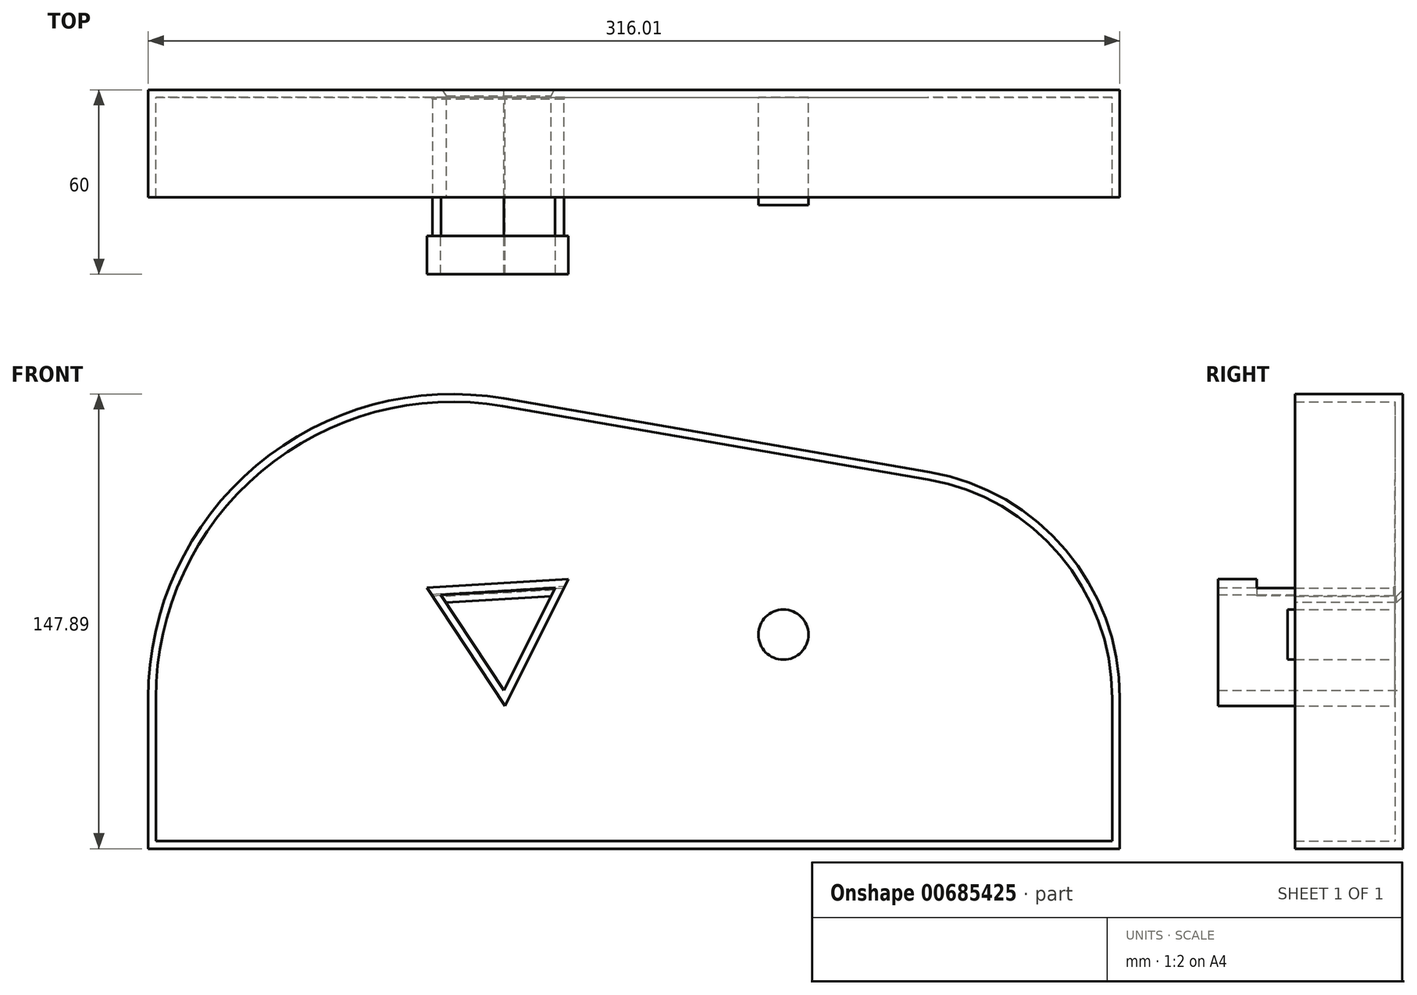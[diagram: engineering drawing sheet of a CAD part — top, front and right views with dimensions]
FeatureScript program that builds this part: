
annotation { "Feature Type Name" : "Feature", "Feature Type Description" : "" }
export const myFeature = defineFeature(function(context is Context, id is Id, definition is map)
    precondition{}
    {
        {
            var Q0;
            Q0=qCreatedBy(makeId("Front.planeOp"),FACE);
            var sketch = newSketch(context, id + "F0", { "sketchPlane" : qUnion([Q0])});
            skCircle(sketch, "E0", {"center": v(0, 0) * mm, "radius": 53.72 * mm});
            skCircle(sketch, "E1", {"center": v(0, 0) * mm, "radius": 58.67 * mm, "construction": true});
            skCircle(sketch, "E2", {"center": v(0, 0) * mm, "radius": 63.5 * mm, "construction": true});
            skLineSegment(sketch, "E3", {"start": v(0, 0) * mm, "end": v(0, 95.44) * mm, "construction": true});
            skLineSegment(sketch, "E4", {"start": v(0, 0) * mm, "end": v(-6.27, 95.6) * mm, "construction": true});
            skLineSegment(sketch, "E5", {"start": v(0, 58.67) * mm, "end": v(-75.4, 58.67) * mm, "construction": true});
            skLineSegment(sketch, "E6", {"start": v(0, 58.67) * mm, "end": v(-75.03, 31.36) * mm, "construction": true});
            skCircle(sketch, "E7", {"center": v(0, 0) * mm, "radius": 55.14 * mm, "construction": true});
            skCircle(sketch, "E8", {"center": v(0, 58.67) * mm, "radius": 14.6 * mm, "construction": true});
            skCircle(sketch, "E9", {"center": v(-13.72, 53.68) * mm, "radius": 14.6 * mm, "construction": true});
            skArc(sketch, "E10", {"start": v(0, 58.67) * mm, "mid": v(-1.15, 61.22) * mm, "end": v(-2.86, 63.44) * mm});
            skArc(sketch, "E11", {"start": v(0.88, 53.71) * mm, "mid": v(0.6, 56.22) * mm, "end": v(0, 58.67) * mm});
            skArc(sketch, "E12.MirrorCS", {"start": v(-7.66, 58.17) * mm, "mid": v(-6.85, 60.85) * mm, "end": v(-5.45, 63.27) * mm});
            skArc(sketch, "E13.MirrorCS", {"start": v(-7.88, 53.14) * mm, "mid": v(-7.94, 55.66) * mm, "end": v(-7.66, 58.17) * mm});
            skArc(sketch, "E14", {"start": v(-2.86, 63.44) * mm, "mid": v(-4.17, 63.7) * mm, "end": v(-5.45, 63.27) * mm});
            skCircle(sketch, "E15", {"center": v(0, 0) * mm, "radius": 30.86 * mm});
            skCircle(sketch, "E16.cCircle", {"center": v(0, 0) * mm, "radius": 10.79 * mm, "construction": true});
            skLineSegment(sketch, "E16.0", {"start": v(18.01, 11.88) * mm, "end": v(1.28, -21.54) * mm});
            skLineSegment(sketch, "E16.1", {"start": v(1.28, -21.54) * mm, "end": v(-19.3, 9.66) * mm});
            skLineSegment(sketch, "E16.2", {"start": v(-19.3, 9.66) * mm, "end": v(18.01, 11.88) * mm});
            skPoint(sketch, "E16.0.midPoint", {"position": v(9.65, -4.83) * mm});
            skSolve(sketch);
        }
        {
            var Q0;
            {var subQ0=sQuery(id+"F0.wireOp",EDGE,"E0");var subQ1=makeQuery(id+"F0.imprint","INTERSECT",VERTEX,{"derivedFrom":[subQ0,sQuery(id+"F0.wireOp",EDGE,"E11")]});Q0=makeQuery(id+"F0.imprint","IMPRINT",FACE,{"disambiguationData":[TD([[makeQuery(id+"F0.imprint","IMPRINT",EDGE,{"disambiguationData":[TD([[subQ1,-1.0]])],"derivedFrom":subQ0}),1.0]])]});}
            var Q1;
            Q1=makeQuery(id+"F0.imprint","IMPRINT",FACE,{"disambiguationData":[TD([[makeQuery(id+"F0.imprint","IMPRINT",EDGE,{"derivedFrom":sQuery(id+"F0.wireOp",EDGE,"E10")}),1.0]])]});
            var Q2;
            Q2=makeQuery(id+"F0.imprint","IMPRINT",FACE,{"disambiguationData":[TD([[makeQuery(id+"F0.imprint","IMPRINT",EDGE,{"derivedFrom":sQuery(id+"F0.wireOp",EDGE,"3Q0PKgbY-dWzt-37Ak-rDaJ-mU9UwyPIQOex")}),1.0]])]});
            var Q3;
            Q3=makeQuery(id+"F0.imprint","IMPRINT",FACE,{"disambiguationData":[TD([[makeQuery(id+"F0.imprint","IMPRINT",EDGE,{"derivedFrom":sQuery(id+"F0.wireOp",EDGE,"4417614c-5319-454a-a1dd-4df527e49696.0")}),-1.0]])]});
            extrude(context, id + "F1", {"entities" : qUnion([Q0, Q1, Q2, Q3]), "depth" : 30 * mm, "offsetDistance" : 25 * mm});
        }
        {
            var Q0;
            Q0=makeQuery(id+"F0.imprint","IMPRINT",FACE,{"disambiguationData":[TD([[makeQuery(id+"F0.imprint","IMPRINT",EDGE,{"derivedFrom":sQuery(id+"F0.wireOp",EDGE,"E15")}),1.0]])]});
            extrude(context, id + "F2", {"entities" : qUnion([Q0]), "operationType" : NewBodyOperationType.ADD, "depth" : 50 * mm, "offsetDistance" : 25 * mm});
        }
        {
            var Q0;
            Q0=makeQuery(id+"F1.opExtrude","CAP_EDGE",EDGE,{"disambiguationData":[OSD([sQuery(id+"F0.wireOp",EDGE,"E11")])],"isStart":false});
            var Q1;
            Q1=makeQuery(id+"F1.opExtrude","CAP_EDGE",EDGE,{"disambiguationData":[OSD([sQuery(id+"F0.wireOp",EDGE,"E13.MirrorCS")])],"isStart":false});
            var Q2;
            Q2=makeQuery(id+"F18UF4900IuEQJn_1.opPattern","COPY",EDGE,{"derivedFrom":makeQuery(id+"F1.opExtrude","CAP_EDGE",EDGE,{"disambiguationData":[OSD([sQuery(id+"F0.wireOp",EDGE,"E13.MirrorCS")])],"isStart":false}),"instanceName":"1"});
            var Q3;
            Q3=makeQuery(id+"F18UF4900IuEQJn_1.opPattern","COPY",EDGE,{"derivedFrom":makeQuery(id+"F1.opExtrude","CAP_EDGE",EDGE,{"disambiguationData":[OSD([sQuery(id+"F0.wireOp",EDGE,"E11")])],"isStart":false}),"instanceName":"1"});
            var Q4;
            Q4=makeQuery(id+"F18UF4900IuEQJn_1.opPattern","COPY",EDGE,{"derivedFrom":makeQuery(id+"F1.opExtrude","CAP_EDGE",EDGE,{"disambiguationData":[OSD([sQuery(id+"F0.wireOp",EDGE,"E13.MirrorCS")])],"isStart":false}),"instanceName":"2"});
            var Q5;
            Q5=makeQuery(id+"F18UF4900IuEQJn_1.opPattern","COPY",EDGE,{"derivedFrom":makeQuery(id+"F1.opExtrude","CAP_EDGE",EDGE,{"disambiguationData":[OSD([sQuery(id+"F0.wireOp",EDGE,"E11")])],"isStart":false}),"instanceName":"2"});
            var Q6;
            Q6=makeQuery(id+"F18UF4900IuEQJn_1.opPattern","COPY",EDGE,{"derivedFrom":makeQuery(id+"F1.opExtrude","CAP_EDGE",EDGE,{"disambiguationData":[OSD([sQuery(id+"F0.wireOp",EDGE,"E13.MirrorCS")])],"isStart":false}),"instanceName":"3"});
            var Q7;
            Q7=makeQuery(id+"F18UF4900IuEQJn_1.opPattern","COPY",EDGE,{"derivedFrom":makeQuery(id+"F1.opExtrude","CAP_EDGE",EDGE,{"disambiguationData":[OSD([sQuery(id+"F0.wireOp",EDGE,"E11")])],"isStart":false}),"instanceName":"3"});
            var Q8;
            Q8=makeQuery(id+"F18UF4900IuEQJn_1.opPattern","COPY",EDGE,{"derivedFrom":makeQuery(id+"F1.opExtrude","CAP_EDGE",EDGE,{"disambiguationData":[OSD([sQuery(id+"F0.wireOp",EDGE,"E13.MirrorCS")])],"isStart":false}),"instanceName":"4"});
            var Q9;
            Q9=makeQuery(id+"F18UF4900IuEQJn_1.opPattern","COPY",EDGE,{"derivedFrom":makeQuery(id+"F1.opExtrude","CAP_EDGE",EDGE,{"disambiguationData":[OSD([sQuery(id+"F0.wireOp",EDGE,"E11")])],"isStart":false}),"instanceName":"4"});
            var Q10;
            Q10=makeQuery(id+"F18UF4900IuEQJn_1.opPattern","COPY",EDGE,{"derivedFrom":makeQuery(id+"F1.opExtrude","CAP_EDGE",EDGE,{"disambiguationData":[OSD([sQuery(id+"F0.wireOp",EDGE,"E13.MirrorCS")])],"isStart":false}),"instanceName":"5"});
            var Q11;
            Q11=makeQuery(id+"F18UF4900IuEQJn_1.opPattern","COPY",EDGE,{"derivedFrom":makeQuery(id+"F1.opExtrude","CAP_EDGE",EDGE,{"disambiguationData":[OSD([sQuery(id+"F0.wireOp",EDGE,"E11")])],"isStart":false}),"instanceName":"5"});
            var Q12;
            Q12=makeQuery(id+"F18UF4900IuEQJn_1.opPattern","COPY",EDGE,{"derivedFrom":makeQuery(id+"F1.opExtrude","CAP_EDGE",EDGE,{"disambiguationData":[OSD([sQuery(id+"F0.wireOp",EDGE,"E13.MirrorCS")])],"isStart":false}),"instanceName":"6"});
            var Q13;
            Q13=makeQuery(id+"F18UF4900IuEQJn_1.opPattern","COPY",EDGE,{"derivedFrom":makeQuery(id+"F1.opExtrude","CAP_EDGE",EDGE,{"disambiguationData":[OSD([sQuery(id+"F0.wireOp",EDGE,"E11")])],"isStart":false}),"instanceName":"6"});
            var Q14;
            Q14=makeQuery(id+"F18UF4900IuEQJn_1.opPattern","COPY",EDGE,{"derivedFrom":makeQuery(id+"F1.opExtrude","CAP_EDGE",EDGE,{"disambiguationData":[OSD([sQuery(id+"F0.wireOp",EDGE,"E13.MirrorCS")])],"isStart":false}),"instanceName":"7"});
            var Q15;
            Q15=makeQuery(id+"F18UF4900IuEQJn_1.opPattern","COPY",EDGE,{"derivedFrom":makeQuery(id+"F1.opExtrude","CAP_EDGE",EDGE,{"disambiguationData":[OSD([sQuery(id+"F0.wireOp",EDGE,"E11")])],"isStart":false}),"instanceName":"7"});
            var Q16;
            Q16=makeQuery(id+"F18UF4900IuEQJn_1.opPattern","COPY",EDGE,{"derivedFrom":makeQuery(id+"F1.opExtrude","CAP_EDGE",EDGE,{"disambiguationData":[OSD([sQuery(id+"F0.wireOp",EDGE,"E13.MirrorCS")])],"isStart":false}),"instanceName":"8"});
            var Q17;
            Q17=makeQuery(id+"F18UF4900IuEQJn_1.opPattern","COPY",EDGE,{"derivedFrom":makeQuery(id+"F1.opExtrude","CAP_EDGE",EDGE,{"disambiguationData":[OSD([sQuery(id+"F0.wireOp",EDGE,"E11")])],"isStart":false}),"instanceName":"8"});
            var Q18;
            Q18=makeQuery(id+"F18UF4900IuEQJn_1.opPattern","COPY",EDGE,{"derivedFrom":makeQuery(id+"F1.opExtrude","SWEPT_EDGE",EDGE,{"disambiguationData":[OSD([sQuery(id+"F0.wireOp",EDGE,"E12.MirrorCS"),sQuery(id+"F0.wireOp",EDGE,"E13.MirrorCS")])]}),"instanceName":"9"});
            var Q19;
            Q19=makeQuery(id+"F18UF4900IuEQJn_1.opPattern","COPY",EDGE,{"derivedFrom":makeQuery(id+"F1.opExtrude","CAP_EDGE",EDGE,{"disambiguationData":[OSD([sQuery(id+"F0.wireOp",EDGE,"E13.MirrorCS")])],"isStart":false}),"instanceName":"9"});
            var Q20;
            Q20=makeQuery(id+"F18UF4900IuEQJn_1.opPattern","COPY",EDGE,{"derivedFrom":makeQuery(id+"F1.opExtrude","CAP_EDGE",EDGE,{"disambiguationData":[OSD([sQuery(id+"F0.wireOp",EDGE,"E11")])],"isStart":false}),"instanceName":"9"});
            var Q21;
            Q21=makeQuery(id+"F18UF4900IuEQJn_1.opPattern","COPY",EDGE,{"derivedFrom":makeQuery(id+"F1.opExtrude","CAP_EDGE",EDGE,{"disambiguationData":[OSD([sQuery(id+"F0.wireOp",EDGE,"E13.MirrorCS")])],"isStart":false}),"instanceName":"10"});
            var Q22;
            Q22=makeQuery(id+"F18UF4900IuEQJn_1.opPattern","COPY",EDGE,{"derivedFrom":makeQuery(id+"F1.opExtrude","CAP_EDGE",EDGE,{"disambiguationData":[OSD([sQuery(id+"F0.wireOp",EDGE,"E11")])],"isStart":false}),"instanceName":"10"});
            var Q23;
            Q23=makeQuery(id+"F18UF4900IuEQJn_1.opPattern","COPY",EDGE,{"derivedFrom":makeQuery(id+"F1.opExtrude","CAP_EDGE",EDGE,{"disambiguationData":[OSD([sQuery(id+"F0.wireOp",EDGE,"E13.MirrorCS")])],"isStart":false}),"instanceName":"11"});
            var Q24;
            Q24=makeQuery(id+"F18UF4900IuEQJn_1.opPattern","COPY",EDGE,{"derivedFrom":makeQuery(id+"F1.opExtrude","CAP_EDGE",EDGE,{"disambiguationData":[OSD([sQuery(id+"F0.wireOp",EDGE,"E11")])],"isStart":false}),"instanceName":"11"});
            var Q25;
            Q25=makeQuery(id+"F18UF4900IuEQJn_1.opPattern","COPY",EDGE,{"derivedFrom":makeQuery(id+"F1.opExtrude","CAP_EDGE",EDGE,{"disambiguationData":[OSD([sQuery(id+"F0.wireOp",EDGE,"E13.MirrorCS")])],"isStart":false}),"instanceName":"12"});
            var Q26;
            Q26=makeQuery(id+"F18UF4900IuEQJn_1.opPattern","COPY",EDGE,{"derivedFrom":makeQuery(id+"F1.opExtrude","CAP_EDGE",EDGE,{"disambiguationData":[OSD([sQuery(id+"F0.wireOp",EDGE,"E11")])],"isStart":false}),"instanceName":"12"});
            var Q27;
            Q27=makeQuery(id+"F18UF4900IuEQJn_1.opPattern","COPY",EDGE,{"derivedFrom":makeQuery(id+"F1.opExtrude","CAP_EDGE",EDGE,{"disambiguationData":[OSD([sQuery(id+"F0.wireOp",EDGE,"E13.MirrorCS")])],"isStart":false}),"instanceName":"13"});
            var Q28;
            Q28=makeQuery(id+"F18UF4900IuEQJn_1.opPattern","COPY",EDGE,{"derivedFrom":makeQuery(id+"F1.opExtrude","CAP_EDGE",EDGE,{"disambiguationData":[OSD([sQuery(id+"F0.wireOp",EDGE,"E11")])],"isStart":false}),"instanceName":"13"});
            var Q29;
            Q29=makeQuery(id+"F18UF4900IuEQJn_1.opPattern","COPY",EDGE,{"derivedFrom":makeQuery(id+"F1.opExtrude","CAP_EDGE",EDGE,{"disambiguationData":[OSD([sQuery(id+"F0.wireOp",EDGE,"E13.MirrorCS")])],"isStart":false}),"instanceName":"14"});
            var Q30;
            Q30=makeQuery(id+"F18UF4900IuEQJn_1.opPattern","COPY",EDGE,{"derivedFrom":makeQuery(id+"F1.opExtrude","CAP_EDGE",EDGE,{"disambiguationData":[OSD([sQuery(id+"F0.wireOp",EDGE,"E11")])],"isStart":false}),"instanceName":"14"});
            var Q31;
            Q31=makeQuery(id+"F18UF4900IuEQJn_1.opPattern","COPY",EDGE,{"derivedFrom":makeQuery(id+"F1.opExtrude","CAP_EDGE",EDGE,{"disambiguationData":[OSD([sQuery(id+"F0.wireOp",EDGE,"E13.MirrorCS")])],"isStart":false}),"instanceName":"15"});
            var Q32;
            Q32=makeQuery(id+"F18UF4900IuEQJn_1.opPattern","COPY",EDGE,{"derivedFrom":makeQuery(id+"F1.opExtrude","CAP_EDGE",EDGE,{"disambiguationData":[OSD([sQuery(id+"F0.wireOp",EDGE,"E11")])],"isStart":false}),"instanceName":"15"});
            var Q33;
            Q33=makeQuery(id+"F18UF4900IuEQJn_1.opPattern","COPY",EDGE,{"derivedFrom":makeQuery(id+"F1.opExtrude","CAP_EDGE",EDGE,{"disambiguationData":[OSD([sQuery(id+"F0.wireOp",EDGE,"E13.MirrorCS")])],"isStart":false}),"instanceName":"16"});
            var Q34;
            Q34=makeQuery(id+"F18UF4900IuEQJn_1.opPattern","COPY",EDGE,{"derivedFrom":makeQuery(id+"F1.opExtrude","CAP_EDGE",EDGE,{"disambiguationData":[OSD([sQuery(id+"F0.wireOp",EDGE,"E11")])],"isStart":false}),"instanceName":"16"});
            var Q35;
            Q35=makeQuery(id+"F18UF4900IuEQJn_1.opPattern","COPY",EDGE,{"derivedFrom":makeQuery(id+"F1.opExtrude","CAP_EDGE",EDGE,{"disambiguationData":[OSD([sQuery(id+"F0.wireOp",EDGE,"E13.MirrorCS")])],"isStart":false}),"instanceName":"17"});
            var Q36;
            Q36=makeQuery(id+"F18UF4900IuEQJn_1.opPattern","COPY",EDGE,{"derivedFrom":makeQuery(id+"F1.opExtrude","CAP_EDGE",EDGE,{"disambiguationData":[OSD([sQuery(id+"F0.wireOp",EDGE,"E11")])],"isStart":false}),"instanceName":"17"});
            var Q37;
            Q37=makeQuery(id+"F18UF4900IuEQJn_1.opPattern","COPY",EDGE,{"derivedFrom":makeQuery(id+"F1.opExtrude","CAP_EDGE",EDGE,{"disambiguationData":[OSD([sQuery(id+"F0.wireOp",EDGE,"E13.MirrorCS")])],"isStart":false}),"instanceName":"18"});
            var Q38;
            Q38=makeQuery(id+"F18UF4900IuEQJn_1.opPattern","COPY",EDGE,{"derivedFrom":makeQuery(id+"F1.opExtrude","CAP_EDGE",EDGE,{"disambiguationData":[OSD([sQuery(id+"F0.wireOp",EDGE,"E11")])],"isStart":false}),"instanceName":"18"});
            var Q39;
            Q39=makeQuery(id+"F18UF4900IuEQJn_1.opPattern","COPY",EDGE,{"derivedFrom":makeQuery(id+"F1.opExtrude","CAP_EDGE",EDGE,{"disambiguationData":[OSD([sQuery(id+"F0.wireOp",EDGE,"E13.MirrorCS")])],"isStart":false}),"instanceName":"19"});
            var Q40;
            Q40=makeQuery(id+"F18UF4900IuEQJn_1.opPattern","COPY",EDGE,{"derivedFrom":makeQuery(id+"F1.opExtrude","CAP_EDGE",EDGE,{"disambiguationData":[OSD([sQuery(id+"F0.wireOp",EDGE,"E11")])],"isStart":false}),"instanceName":"19"});
            var Q41;
            Q41=makeQuery(id+"F18UF4900IuEQJn_1.opPattern","COPY",EDGE,{"derivedFrom":makeQuery(id+"F1.opExtrude","CAP_EDGE",EDGE,{"disambiguationData":[OSD([sQuery(id+"F0.wireOp",EDGE,"E13.MirrorCS")])],"isStart":false}),"instanceName":"20"});
            var Q42;
            Q42=makeQuery(id+"F18UF4900IuEQJn_1.opPattern","COPY",EDGE,{"derivedFrom":makeQuery(id+"F1.opExtrude","CAP_EDGE",EDGE,{"disambiguationData":[OSD([sQuery(id+"F0.wireOp",EDGE,"E11")])],"isStart":false}),"instanceName":"20"});
            var Q43;
            Q43=makeQuery(id+"F18UF4900IuEQJn_1.opPattern","COPY",EDGE,{"derivedFrom":makeQuery(id+"F1.opExtrude","CAP_EDGE",EDGE,{"disambiguationData":[OSD([sQuery(id+"F0.wireOp",EDGE,"E13.MirrorCS")])],"isStart":false}),"instanceName":"21"});
            var Q44;
            Q44=makeQuery(id+"F18UF4900IuEQJn_1.opPattern","COPY",EDGE,{"derivedFrom":makeQuery(id+"F1.opExtrude","CAP_EDGE",EDGE,{"disambiguationData":[OSD([sQuery(id+"F0.wireOp",EDGE,"E11")])],"isStart":false}),"instanceName":"21"});
            var Q45;
            Q45=makeQuery(id+"F18UF4900IuEQJn_1.opPattern","COPY",EDGE,{"derivedFrom":makeQuery(id+"F1.opExtrude","CAP_EDGE",EDGE,{"disambiguationData":[OSD([sQuery(id+"F0.wireOp",EDGE,"E13.MirrorCS")])],"isStart":false}),"instanceName":"22"});
            var Q46;
            Q46=makeQuery(id+"F18UF4900IuEQJn_1.opPattern","COPY",EDGE,{"derivedFrom":makeQuery(id+"F1.opExtrude","CAP_EDGE",EDGE,{"disambiguationData":[OSD([sQuery(id+"F0.wireOp",EDGE,"E11")])],"isStart":false}),"instanceName":"22"});
            var Q47;
            Q47=makeQuery(id+"F18UF4900IuEQJn_1.opPattern","COPY",EDGE,{"derivedFrom":makeQuery(id+"F1.opExtrude","CAP_EDGE",EDGE,{"disambiguationData":[OSD([sQuery(id+"F0.wireOp",EDGE,"E13.MirrorCS")])],"isStart":false}),"instanceName":"23"});
            var Q48;
            Q48=makeQuery(id+"F18UF4900IuEQJn_1.opPattern","COPY",EDGE,{"derivedFrom":makeQuery(id+"F1.opExtrude","CAP_EDGE",EDGE,{"disambiguationData":[OSD([sQuery(id+"F0.wireOp",EDGE,"E11")])],"isStart":false}),"instanceName":"23"});
            var Q49;
            {var subQ0=sQuery(id+"F0.wireOp",EDGE,"E15");var subQ1=makeQuery(id+"F1.opExtrude","CAP_FACE",FACE,{"disambiguationData":[OSD([sQuery(id+"F0.wireOp",EDGE,"E0"),sQuery(id+"F0.wireOp",EDGE,"E10"),sQuery(id+"F0.wireOp",EDGE,"E11"),sQuery(id+"F0.wireOp",EDGE,"E12.MirrorCS"),sQuery(id+"F0.wireOp",EDGE,"E13.MirrorCS"),sQuery(id+"F0.wireOp",EDGE,"E14"),subQ0])],"isStart":true});Q49=makeQuery(id+"F2.boolean.opBoolean","MERGE",FACE,{"derivedFrom":[subQ1,makeQuery(id+"F18UF4900IuEQJn_1.opPattern","COPY",FACE,{"derivedFrom":subQ1,"instanceName":"1"}),makeQuery(id+"F18UF4900IuEQJn_1.opPattern","COPY",FACE,{"derivedFrom":subQ1,"instanceName":"2"}),makeQuery(id+"F18UF4900IuEQJn_1.opPattern","COPY",FACE,{"derivedFrom":subQ1,"instanceName":"3"}),makeQuery(id+"F18UF4900IuEQJn_1.opPattern","COPY",FACE,{"derivedFrom":subQ1,"instanceName":"4"}),makeQuery(id+"F18UF4900IuEQJn_1.opPattern","COPY",FACE,{"derivedFrom":subQ1,"instanceName":"5"}),makeQuery(id+"F18UF4900IuEQJn_1.opPattern","COPY",FACE,{"derivedFrom":subQ1,"instanceName":"6"}),makeQuery(id+"F18UF4900IuEQJn_1.opPattern","COPY",FACE,{"derivedFrom":subQ1,"instanceName":"7"}),makeQuery(id+"F18UF4900IuEQJn_1.opPattern","COPY",FACE,{"derivedFrom":subQ1,"instanceName":"8"}),makeQuery(id+"F18UF4900IuEQJn_1.opPattern","COPY",FACE,{"derivedFrom":subQ1,"instanceName":"9"}),makeQuery(id+"F18UF4900IuEQJn_1.opPattern","COPY",FACE,{"derivedFrom":subQ1,"instanceName":"10"}),makeQuery(id+"F18UF4900IuEQJn_1.opPattern","COPY",FACE,{"derivedFrom":subQ1,"instanceName":"11"}),makeQuery(id+"F18UF4900IuEQJn_1.opPattern","COPY",FACE,{"derivedFrom":subQ1,"instanceName":"12"}),makeQuery(id+"F18UF4900IuEQJn_1.opPattern","COPY",FACE,{"derivedFrom":subQ1,"instanceName":"13"}),makeQuery(id+"F18UF4900IuEQJn_1.opPattern","COPY",FACE,{"derivedFrom":subQ1,"instanceName":"14"}),makeQuery(id+"F18UF4900IuEQJn_1.opPattern","COPY",FACE,{"derivedFrom":subQ1,"instanceName":"15"}),makeQuery(id+"F18UF4900IuEQJn_1.opPattern","COPY",FACE,{"derivedFrom":subQ1,"instanceName":"16"}),makeQuery(id+"F18UF4900IuEQJn_1.opPattern","COPY",FACE,{"derivedFrom":subQ1,"instanceName":"17"}),makeQuery(id+"F18UF4900IuEQJn_1.opPattern","COPY",FACE,{"derivedFrom":subQ1,"instanceName":"18"}),makeQuery(id+"F18UF4900IuEQJn_1.opPattern","COPY",FACE,{"derivedFrom":subQ1,"instanceName":"19"}),makeQuery(id+"F18UF4900IuEQJn_1.opPattern","COPY",FACE,{"derivedFrom":subQ1,"instanceName":"20"}),makeQuery(id+"F18UF4900IuEQJn_1.opPattern","COPY",FACE,{"derivedFrom":subQ1,"instanceName":"21"}),makeQuery(id+"F18UF4900IuEQJn_1.opPattern","COPY",FACE,{"derivedFrom":subQ1,"instanceName":"22"}),makeQuery(id+"F18UF4900IuEQJn_1.opPattern","COPY",FACE,{"derivedFrom":subQ1,"instanceName":"23"}),makeQuery(id+"F2.opExtrude","CAP_FACE",FACE,{"disambiguationData":[OSD([sQuery(id+"F0.wireOp",EDGE,"19ae24a6-e92d-4116-b942-5415395ed2d1.0"),sQuery(id+"F0.wireOp",EDGE,"19ae24a6-e92d-4116-b942-5415395ed2d1.1"),sQuery(id+"F0.wireOp",EDGE,"19ae24a6-e92d-4116-b942-5415395ed2d1.2"),sQuery(id+"F0.wireOp",EDGE,"19ae24a6-e92d-4116-b942-5415395ed2d1.3"),sQuery(id+"F0.wireOp",EDGE,"19ae24a6-e92d-4116-b942-5415395ed2d1.4"),subQ0])],"isStart":true})]});}
            chamfer(context, id + "F3", {"entities" : qUnion([Q0, Q1, Q2, Q3, Q4, Q5, Q6, Q7, Q8, Q9, Q10, Q11, Q12, Q13, Q14, Q15, Q16, Q17, Q18, Q19, Q20, Q21, Q22, Q23, Q24, Q25, Q26, Q27, Q28, Q29, Q30, Q31, Q32, Q33, Q34, Q35, Q36, Q37, Q38, Q39, Q40, Q41, Q42, Q43, Q44, Q45, Q46, Q47, Q48, Q49]), "width" : 2 * mm, "tangentPropagation" : true});
        }
        {
            var Q0;
            Q0=qCreatedBy(makeId("Front.planeOp"),FACE);
            var sketch = newSketch(context, id + "F4", { "sketchPlane" : qUnion([Q0])});
            skLineSegment(sketch, "E17", {"start": v(-115.72, -21.35) * mm, "end": v(-115.72, -70.35) * mm});
            skLineSegment(sketch, "E18", {"start": v(-115.72, -70.35) * mm, "end": v(200.3, -70.35) * mm});
            skLineSegment(sketch, "E19", {"start": v(200.3, -70.35) * mm, "end": v(200.3, -21.35) * mm});
            skArc(sketch, "E20", {"start": v(0, 76.1) * mm, "mid": v(-80.53, 54.3) * mm, "end": v(-115.72, -21.35) * mm});
            skLineSegment(sketch, "E21", {"start": v(0, 76.1) * mm, "end": v(138.36, 52.2) * mm});
            skArc(sketch, "E22", {"start": v(200.3, -21.35) * mm, "mid": v(182.75, 26.73) * mm, "end": v(138.36, 52.2) * mm});
            skLineSegment(sketch, "E23.0", {"start": v(16.73, 14.55) * mm, "end": v(0, -18.87) * mm});
            skLineSegment(sketch, "E23.1", {"start": v(0, -18.87) * mm, "end": v(-20.58, 12.33) * mm});
            skLineSegment(sketch, "E23.2", {"start": v(-20.58, 12.33) * mm, "end": v(16.73, 14.55) * mm});
            skSolve(sketch);
        }
        {
            var Q0;
            Q0=makeQuery(id+"F4.imprint","IMPRINT",FACE,{"disambiguationData":[TD([[makeQuery(id+"F4.imprint","IMPRINT",EDGE,{"derivedFrom":sQuery(id+"F4.wireOp",EDGE,"E17")}),1.0]])]});
            extrude(context, id + "F5", {"entities" : qUnion([Q0]), "operationType" : NewBodyOperationType.ADD, "depth" : 60 * mm, "offsetDistance" : 25 * mm});
        }
        {
            var Q0;
            Q0=makeQuery(id+"F5.opExtrude","CAP_FACE",FACE,{"disambiguationData":[OSD([sQuery(id+"F4.wireOp",EDGE,"E17"),sQuery(id+"F4.wireOp",EDGE,"E18"),sQuery(id+"F4.wireOp",EDGE,"E19"),sQuery(id+"F4.wireOp",EDGE,"E20"),sQuery(id+"F4.wireOp",EDGE,"E21"),sQuery(id+"F4.wireOp",EDGE,"E22"),sQuery(id+"F4.wireOp",EDGE,"E23.0"),sQuery(id+"F4.wireOp",EDGE,"E23.1"),sQuery(id+"F4.wireOp",EDGE,"E23.2")])],"isStart":false});
            shell(context, id + "F6", {"entities" : qUnion([Q0]), "thickness" : 2.5 * mm});
        }
        {
            var Q0;
            Q0=makeQuery(id+"F2.opExtrude","CAP_FACE",FACE,{"disambiguationData":[OSD([sQuery(id+"F0.wireOp",EDGE,"E15"),sQuery(id+"F0.wireOp",EDGE,"E16.0"),sQuery(id+"F0.wireOp",EDGE,"E16.1"),sQuery(id+"F0.wireOp",EDGE,"E16.2")])],"isStart":false});
            extrude(context, id + "F7", {"entities" : qUnion([Q0]), "operationType" : NewBodyOperationType.REMOVE, "oppositeDirection" : true, "depth" : 15 * mm, "offsetDistance" : 25 * mm});
        }
        {
            var Q0;
            Q0=makeQuery(id+"F5.opExtrude","CAP_FACE",FACE,{"disambiguationData":[OSD([sQuery(id+"F4.wireOp",EDGE,"E17"),sQuery(id+"F4.wireOp",EDGE,"E18"),sQuery(id+"F4.wireOp",EDGE,"E19"),sQuery(id+"F4.wireOp",EDGE,"E20"),sQuery(id+"F4.wireOp",EDGE,"E21"),sQuery(id+"F4.wireOp",EDGE,"E22"),sQuery(id+"F4.wireOp",EDGE,"E23.0"),sQuery(id+"F4.wireOp",EDGE,"E23.1"),sQuery(id+"F4.wireOp",EDGE,"E23.2")])],"isStart":false});
            extrude(context, id + "F8", {"entities" : qUnion([Q0]), "operationType" : NewBodyOperationType.REMOVE, "oppositeDirection" : true, "depth" : 25 * mm, "offsetDistance" : 25 * mm});
        }
        {
            var Q0;
            Q0=makeQuery(id+"F6.opShell","OFFSET_FACE",FACE,{"disambiguationData":[OSD([sQuery(id+"F0.wireOp",EDGE,"E0"),sQuery(id+"F0.wireOp",EDGE,"E10"),sQuery(id+"F0.wireOp",EDGE,"E11"),sQuery(id+"F0.wireOp",EDGE,"E12.MirrorCS"),sQuery(id+"F0.wireOp",EDGE,"E13.MirrorCS"),sQuery(id+"F0.wireOp",EDGE,"E14"),sQuery(id+"F0.wireOp",EDGE,"E15"),sQuery(id+"F0.wireOp",EDGE,"E16.0"),sQuery(id+"F0.wireOp",EDGE,"E16.1"),sQuery(id+"F0.wireOp",EDGE,"E16.2"),sQuery(id+"F4.wireOp",EDGE,"E17"),sQuery(id+"F4.wireOp",EDGE,"E18"),sQuery(id+"F4.wireOp",EDGE,"E19"),sQuery(id+"F4.wireOp",EDGE,"E20"),sQuery(id+"F4.wireOp",EDGE,"E21"),sQuery(id+"F4.wireOp",EDGE,"E22"),sQuery(id+"F4.wireOp",EDGE,"E23.0"),sQuery(id+"F4.wireOp",EDGE,"E23.1"),sQuery(id+"F4.wireOp",EDGE,"E23.2")])]});
            var sketch = newSketch(context, id + "F9", { "sketchPlane" : qUnion([Q0])});
            skCircle(sketch, "E24", {"center": v(90.87, -0.7) * mm, "radius": 8.15 * mm});
            skSolve(sketch);
        }
        {
            var Q0;
            Q0=makeQuery(id+"F9.imprint","IMPRINT",FACE,{"disambiguationData":[TD([[makeQuery(id+"F9.imprint","IMPRINT",EDGE,{"derivedFrom":sQuery(id+"F9.wireOp",EDGE,"E24")}),1.0]])]});
            extrude(context, id + "F10", {"entities" : qUnion([Q0]), "operationType" : NewBodyOperationType.ADD, "depth" : 35 * mm, "offsetDistance" : 25 * mm});
        }
    });
